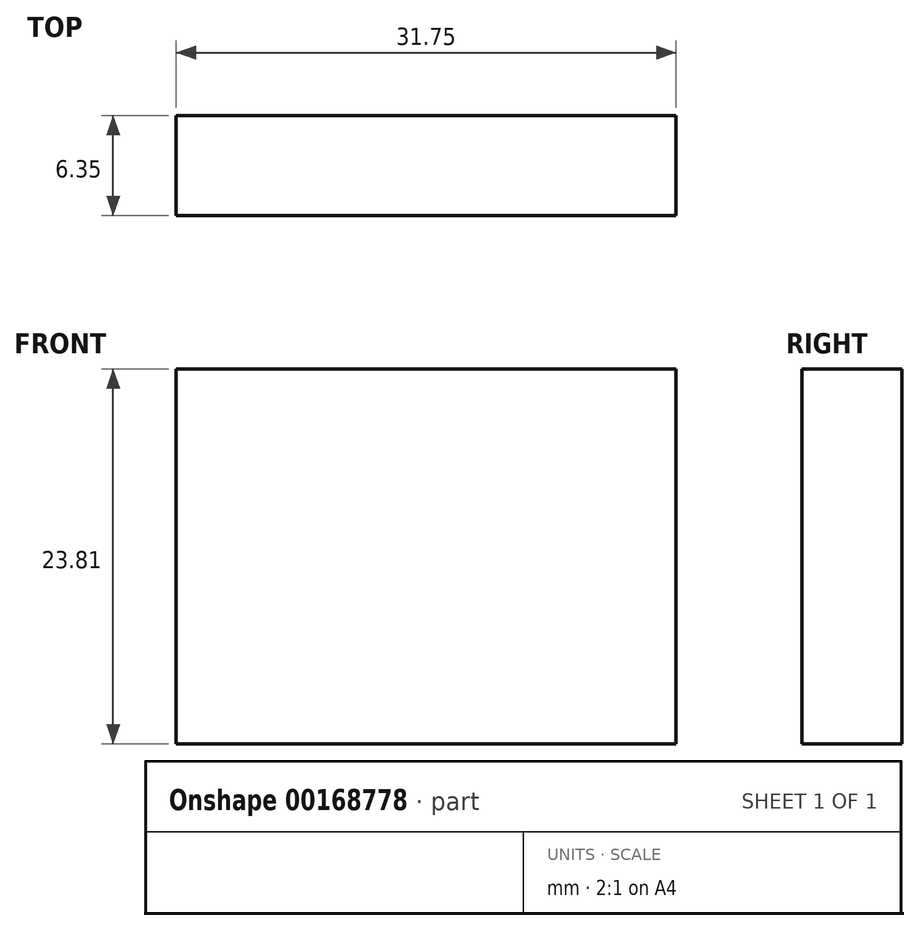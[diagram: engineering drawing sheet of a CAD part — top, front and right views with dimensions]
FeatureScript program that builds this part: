
annotation { "Feature Type Name" : "Feature", "Feature Type Description" : "" }
export const myFeature = defineFeature(function(context is Context, id is Id, definition is map)
    precondition{}
    {
        {
            var Q0;
            Q0=qCreatedBy(makeId("Front.planeOp"),FACE);
            var sketch = newSketch(context, id + "F0", { "sketchPlane" : qUnion([Q0])});
            skLineSegment(sketch, "E0.bottom", {"start": v(-19.2, 17.51) * mm, "end": v(12.55, 17.51) * mm});
            skLineSegment(sketch, "E0.top", {"start": v(-19.2, -7.89) * mm, "end": v(12.55, -7.89) * mm});
            skLineSegment(sketch, "E0.left", {"start": v(-19.2, 17.51) * mm, "end": v(-19.2, -7.89) * mm});
            skLineSegment(sketch, "E0.right", {"start": v(12.55, 17.51) * mm, "end": v(12.55, -7.89) * mm});
            skLineSegment(sketch, "E1", {"start": v(-19.2, 15.92) * mm, "end": v(12.55, 15.92) * mm});
            skLineSegment(sketch, "E2.1.0.0", {"start": v(-19.2, 14.34) * mm, "end": v(12.55, 14.34) * mm});
            skLineSegment(sketch, "E2.2.0.0", {"start": v(-19.2, 12.75) * mm, "end": v(12.55, 12.75) * mm});
            skLineSegment(sketch, "E2.3.0.0", {"start": v(-19.2, 11.16) * mm, "end": v(12.55, 11.16) * mm});
            skLineSegment(sketch, "E2.4.0.0", {"start": v(-19.2, 9.57) * mm, "end": v(12.55, 9.57) * mm});
            skLineSegment(sketch, "E2.5.0.0", {"start": v(-19.2, 7.99) * mm, "end": v(12.55, 7.99) * mm});
            skLineSegment(sketch, "E2.6.0.0", {"start": v(-19.2, 6.4) * mm, "end": v(12.55, 6.4) * mm});
            skLineSegment(sketch, "E2.7.0.0", {"start": v(-19.2, 4.81) * mm, "end": v(12.55, 4.81) * mm});
            skLineSegment(sketch, "E2.8.0.0", {"start": v(-19.2, 3.22) * mm, "end": v(12.55, 3.22) * mm});
            skLineSegment(sketch, "E2.9.0.0", {"start": v(-19.2, 1.64) * mm, "end": v(12.55, 1.64) * mm});
            skLineSegment(sketch, "E2.10.0.0", {"start": v(-19.2, 0.05) * mm, "end": v(12.55, 0.05) * mm});
            skLineSegment(sketch, "E2.11.0.0", {"start": v(-19.2, -1.54) * mm, "end": v(12.55, -1.54) * mm});
            skLineSegment(sketch, "E2.12.0.0", {"start": v(-19.2, -3.13) * mm, "end": v(12.56, -3.13) * mm});
            skLineSegment(sketch, "E2.13.0.0", {"start": v(-19.2, -4.71) * mm, "end": v(12.56, -4.71) * mm});
            skLineSegment(sketch, "E2.14.0.0", {"start": v(-19.2, -6.3) * mm, "end": v(12.56, -6.3) * mm});
            skLineSegment(sketch, "E2.direction1", {"start": v(-19.2, 15.92) * mm, "end": v(-19.2, 14.34) * mm, "construction": true});
            skSolve(sketch);
        }
        {
            var Q0;
            Q0 = qSketchRegion(id + "F0", true);
            var Q1;
            Q1=sQuery(id+"F0.wireOp",EDGE,"E1");
            var Q2;
            Q2=sQuery(id+"F0.wireOp",EDGE,"E2.1.0.0");
            var Q3;
            Q3=sQuery(id+"F0.wireOp",EDGE,"E2.2.0.0");
            var Q4;
            Q4=sQuery(id+"F0.wireOp",EDGE,"E2.3.0.0");
            var Q5;
            Q5=sQuery(id+"F0.wireOp",EDGE,"E2.4.0.0");
            var Q6;
            Q6=sQuery(id+"F0.wireOp",EDGE,"E2.5.0.0");
            var Q7;
            Q7=sQuery(id+"F0.wireOp",EDGE,"E2.6.0.0");
            var Q8;
            Q8=sQuery(id+"F0.wireOp",EDGE,"E2.7.0.0");
            var Q9;
            Q9=sQuery(id+"F0.wireOp",EDGE,"E2.8.0.0");
            var Q10;
            Q10=sQuery(id+"F0.wireOp",EDGE,"E2.9.0.0");
            var Q11;
            Q11=sQuery(id+"F0.wireOp",EDGE,"E2.10.0.0");
            var Q12;
            Q12=sQuery(id+"F0.wireOp",EDGE,"E2.11.0.0");
            var Q13;
            Q13=sQuery(id+"F0.wireOp",EDGE,"E2.12.0.0");
            var Q14;
            Q14=sQuery(id+"F0.wireOp",EDGE,"E2.13.0.0");
            var Q15;
            Q15=sQuery(id+"F0.wireOp",EDGE,"E2.14.0.0");
            extrude(context, id + "F1", {"entities" : qUnion([Q0]), "bodyType" : ToolBodyType.SURFACE, "surfaceEntities" : qUnion([Q1, Q2, Q3, Q4, Q5, Q6, Q7, Q8, Q9, Q10, Q11, Q12, Q13, Q14, Q15]), "depth" : 6.35 * mm});
        }
        {
            var Q0;
            Q0=qCreatedBy(makeId("Front.planeOp"),FACE);
            var sketch = newSketch(context, id + "F2", { "sketchPlane" : qUnion([Q0])});
            skCircle(sketch, "E3", {"center": v(-56.4, 17.92) * mm, "radius": 3.18 * mm});
            skSolve(sketch);
        }
        {
            var Q0;
            Q0=sQuery(id+"F2.wireOp",EDGE,"E3");
            extrude(context, id + "F3", {"bodyType" : ToolBodyType.SURFACE, "surfaceEntities" : qUnion([Q0]), "depth" : 12.7 * mm});
        }
        {
            var Q0;
            {var subQ0=sQuery(id+"F0.wireOp",EDGE,"E0.top");Q0=makeQuery(id+"F0.imprint","IMPRINT",FACE,{"disambiguationData":[TD([[makeQuery(id+"F0.imprint","IMPRINT",EDGE,{"derivedFrom":subQ0}),1.0]])]});}
            extrude(context, id + "F4", {"entities" : qUnion([Q0]), "depth" : 6.35 * mm});
        }
    });
